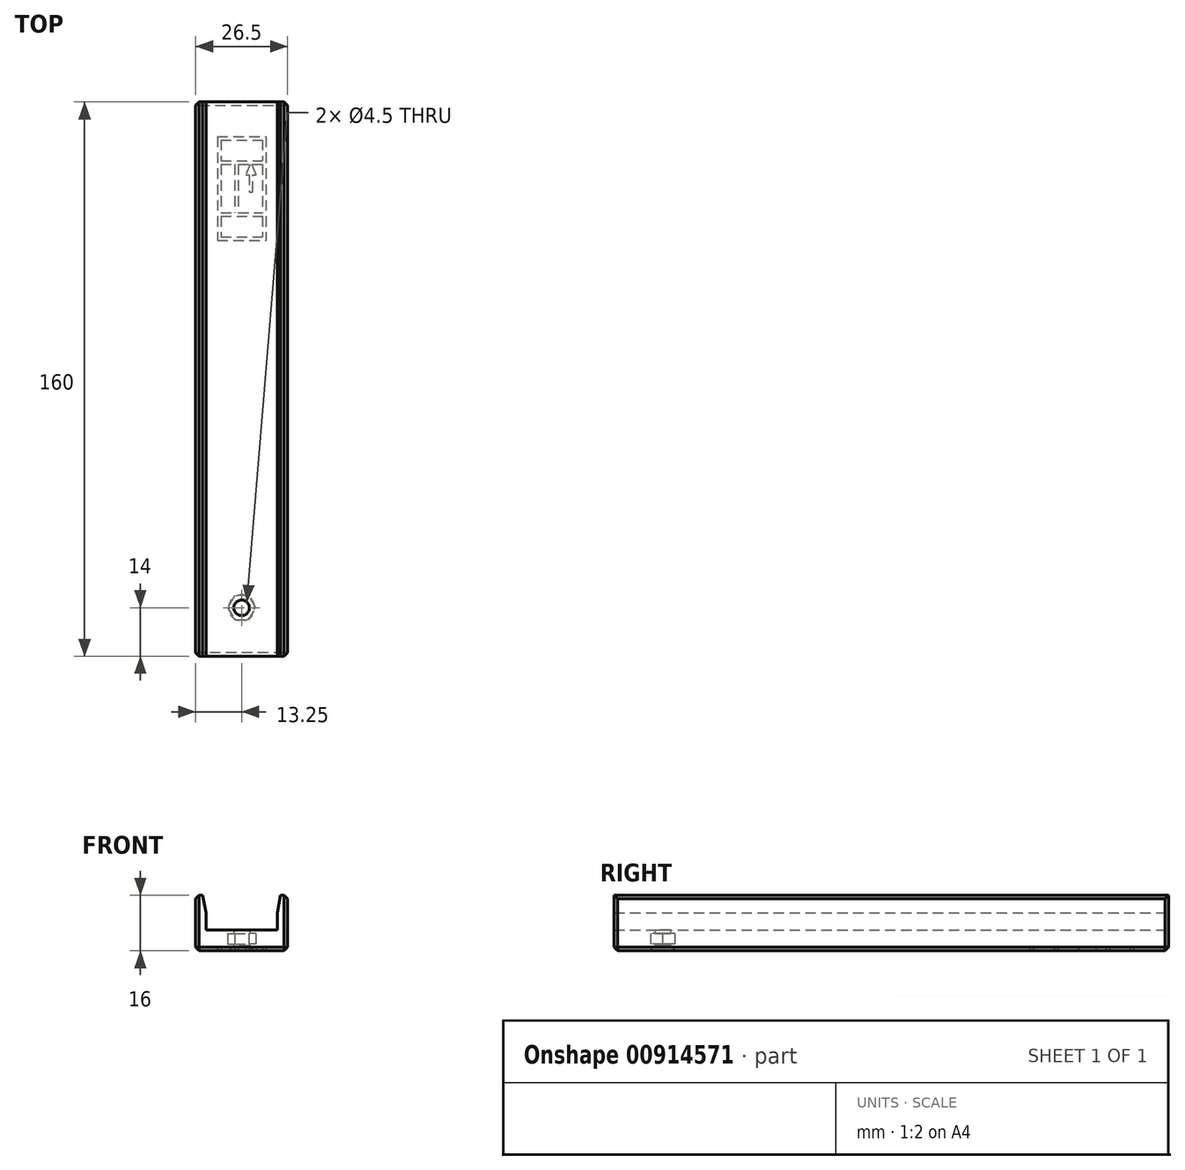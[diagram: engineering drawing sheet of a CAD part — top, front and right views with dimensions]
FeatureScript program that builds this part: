
annotation { "Feature Type Name" : "Feature", "Feature Type Description" : "" }
export const myFeature = defineFeature(function(context is Context, id is Id, definition is map)
    precondition{}
    {
        {
            var Q0;
            Q0=qCreatedBy(makeId("Front.planeOp"),FACE);
            var sketch = newSketch(context, id + "F0", { "sketchPlane" : qUnion([Q0])});
            skLineSegment(sketch, "E0", {"start": v(0, 0) * mm, "end": v(26.5, 0) * mm});
            skLineSegment(sketch, "E1", {"start": v(26.5, 0) * mm, "end": v(26.5, 16) * mm});
            skLineSegment(sketch, "E2", {"start": v(26.5, 16) * mm, "end": v(23.5, 16) * mm});
            skLineSegment(sketch, "E3", {"start": v(23.5, 16) * mm, "end": v(23.5, 6) * mm});
            skLineSegment(sketch, "E4", {"start": v(23.5, 6) * mm, "end": v(3, 6) * mm});
            skLineSegment(sketch, "E5", {"start": v(3, 6) * mm, "end": v(3, 16) * mm});
            skLineSegment(sketch, "E6", {"start": v(3, 16) * mm, "end": v(0, 16) * mm});
            skLineSegment(sketch, "E7", {"start": v(0, 16) * mm, "end": v(0, 0) * mm});
            skSolve(sketch);
        }
        {
            var Q0;
            Q0=qSketchRegion(id+"F0",true);
            extrude(context, id + "F1", {"entities" : qUnion([Q0]), "depth" : 160 * mm, "offsetDistance" : 25 * mm});
        }
        {
            var Q0;
            Q0=makeQuery(id+"F1.opExtrude","SWEPT_FACE",FACE,{"disambiguationData":[OSD([sQuery(id+"F0.wireOp",EDGE,"E0")])]});
            var sketch = newSketch(context, id + "F2", { "sketchPlane" : qUnion([Q0])});
            skCircle(sketch, "E8", {"center": v(13.25, 146) * mm, "radius": 2.25 * mm});
            skSolve(sketch);
        }
        {
            var Q0;
            Q0=qSketchRegion(id+"F2",true);
            extrude(context, id + "F3", {"entities" : qUnion([Q0]), "operationType" : NewBodyOperationType.REMOVE, "endBound" : BoundingType.THROUGH_ALL, "oppositeDirection" : true, "depth" : 25 * mm, "offsetDistance" : 25 * mm});
        }
        {
            var Q0;
            Q0=makeQuery(id+"F1.opExtrude","SWEPT_EDGE",EDGE,{"disambiguationData":[OSD([sQuery(id+"F0.wireOp",EDGE,"E2"),sQuery(id+"F0.wireOp",EDGE,"E3")])]});
            chamfer(context, id + "F4", {"entities" : qUnion([Q0]), "chamferType" : ChamferType.TWO_OFFSETS, "width1" : 5 * mm, "oppositeDirection" : false, "width2" : 1 * mm, "tangentPropagation" : true});
        }
        {
            var Q0;
            Q0=makeQuery(id+"F1.opExtrude","SWEPT_EDGE",EDGE,{"disambiguationData":[OSD([sQuery(id+"F0.wireOp",EDGE,"E5"),sQuery(id+"F0.wireOp",EDGE,"E6")])]});
            chamfer(context, id + "F5", {"entities" : qUnion([Q0]), "chamferType" : ChamferType.TWO_OFFSETS, "width1" : 1 * mm, "oppositeDirection" : false, "width2" : 5 * mm, "tangentPropagation" : true});
        }
        {
            var Q0;
            Q0=makeQuery(id+"F1.opExtrude","SWEPT_FACE",FACE,{"disambiguationData":[OSD([sQuery(id+"F0.wireOp",EDGE,"E0")])]});
            var sketch = newSketch(context, id + "F6", { "sketchPlane" : qUnion([Q0])});
            skCircle(sketch, "E9.cCircle", {"center": v(13.25, 146) * mm, "radius": 3.5 * mm, "construction": true});
            skLineSegment(sketch, "E9.0", {"start": v(11.23, 149.5) * mm, "end": v(15.27, 149.5) * mm});
            skLineSegment(sketch, "E9.1", {"start": v(15.27, 149.5) * mm, "end": v(17.3, 146) * mm});
            skLineSegment(sketch, "E9.2", {"start": v(17.3, 146) * mm, "end": v(15.27, 142.5) * mm});
            skLineSegment(sketch, "E9.3", {"start": v(15.27, 142.5) * mm, "end": v(11.23, 142.5) * mm});
            skLineSegment(sketch, "E9.4", {"start": v(11.23, 142.5) * mm, "end": v(9.2, 146) * mm});
            skLineSegment(sketch, "E9.5", {"start": v(9.2, 146) * mm, "end": v(11.23, 149.5) * mm});
            skPoint(sketch, "E9.0.midPoint", {"position": v(13.25, 149.5) * mm});
            skSolve(sketch);
        }
        {
            var Q0;
            Q0=qSketchRegion(id+"F6",true);
            extrude(context, id + "F7", {"entities" : qUnion([Q0]), "operationType" : NewBodyOperationType.REMOVE, "oppositeDirection" : true, "depth" : 5 * mm, "offsetDistance" : 25 * mm});
        }
        {
            var Q0;
            Q0=makeQuery(id+"F1.opExtrude","SWEPT_FACE",FACE,{"disambiguationData":[OSD([sQuery(id+"F0.wireOp",EDGE,"E0")])]});
            var sketch = newSketch(context, id + "F8", { "sketchPlane" : qUnion([Q0])});
            skCircle(sketch, "E10.cCircle", {"center": v(13.25, 146) * mm, "radius": 3.5 * mm, "construction": true});
            skLineSegment(sketch, "E10.0", {"start": v(11.23, 149.5) * mm, "end": v(15.27, 149.5) * mm});
            skLineSegment(sketch, "E10.1", {"start": v(15.27, 149.5) * mm, "end": v(17.3, 146) * mm});
            skLineSegment(sketch, "E10.2", {"start": v(17.3, 146) * mm, "end": v(15.27, 142.5) * mm});
            skLineSegment(sketch, "E10.3", {"start": v(15.27, 142.5) * mm, "end": v(11.23, 142.5) * mm});
            skLineSegment(sketch, "E10.4", {"start": v(11.23, 142.5) * mm, "end": v(9.2, 146) * mm});
            skLineSegment(sketch, "E10.5", {"start": v(9.2, 146) * mm, "end": v(11.23, 149.5) * mm});
            skPoint(sketch, "E10.0.midPoint", {"position": v(13.25, 149.5) * mm});
            skCircle(sketch, "E11", {"center": v(13.25, 146) * mm, "radius": 2.25 * mm});
            skSolve(sketch);
        }
        {
            var Q0;
            Q0=qSketchRegion(id+"F8",true);
            extrude(context, id + "F9", {"entities" : qUnion([Q0]), "operationType" : NewBodyOperationType.ADD, "oppositeDirection" : true, "depth" : 2 * mm, "offsetDistance" : 25 * mm});
        }
        {
            var Q0;
            Q0=makeQuery(id+"F9.opExtrude","CAP_EDGE",EDGE,{"disambiguationData":[OSD([sQuery(id+"F8.wireOp",EDGE,"E11")])],"isStart":true});
            var Q1;
            Q1=makeQuery(id+"F9.opExtrude","CAP_EDGE",EDGE,{"disambiguationData":[OSD([sQuery(id+"F8.wireOp",EDGE,"b76391ad-7746-4877-8ef7-7a4a0ac5d2b5")])],"isStart":true});
            chamfer(context, id + "F10", {"entities" : qUnion([Q0, Q1]), "width" : 1.5 * mm, "tangentPropagation" : true});
        }
        {
            var Q0;
            Q0=makeQuery(id+"F1.opExtrude","SWEPT_EDGE",EDGE,{"disambiguationData":[OSD([sQuery(id+"F0.wireOp",EDGE,"E0"),sQuery(id+"F0.wireOp",EDGE,"E7")])]});
            var Q1;
            Q1=makeQuery(id+"F1.opExtrude","CAP_EDGE",EDGE,{"disambiguationData":[OSD([sQuery(id+"F0.wireOp",EDGE,"E0")])],"isStart":true});
            var Q2;
            Q2=makeQuery(id+"F1.opExtrude","SWEPT_EDGE",EDGE,{"disambiguationData":[OSD([sQuery(id+"F0.wireOp",EDGE,"E0"),sQuery(id+"F0.wireOp",EDGE,"E1")])]});
            var Q3;
            Q3=makeQuery(id+"F1.opExtrude","CAP_EDGE",EDGE,{"disambiguationData":[OSD([sQuery(id+"F0.wireOp",EDGE,"E0")])],"isStart":false});
            var Q4;
            Q4=makeQuery(id+"F1.opExtrude","CAP_EDGE",EDGE,{"disambiguationData":[OSD([sQuery(id+"F0.wireOp",EDGE,"E7")])],"isStart":true});
            var Q5;
            Q5=makeQuery(id+"F1.opExtrude","CAP_EDGE",EDGE,{"disambiguationData":[OSD([sQuery(id+"F0.wireOp",EDGE,"E1")])],"isStart":true});
            var Q6;
            Q6=makeQuery(id+"F1.opExtrude","CAP_EDGE",EDGE,{"disambiguationData":[OSD([sQuery(id+"F0.wireOp",EDGE,"E7")])],"isStart":false});
            var Q7;
            Q7=makeQuery(id+"F1.opExtrude","CAP_EDGE",EDGE,{"disambiguationData":[OSD([sQuery(id+"F0.wireOp",EDGE,"E1")])],"isStart":false});
            var Q8;
            Q8=makeQuery(id+"F1.opExtrude","SWEPT_EDGE",EDGE,{"disambiguationData":[OSD([sQuery(id+"F0.wireOp",EDGE,"E1"),sQuery(id+"F0.wireOp",EDGE,"E2")])]});
            var Q9;
            Q9=makeQuery(id+"F1.opExtrude","SWEPT_EDGE",EDGE,{"disambiguationData":[OSD([sQuery(id+"F0.wireOp",EDGE,"E6"),sQuery(id+"F0.wireOp",EDGE,"E7")])]});
            chamfer(context, id + "F11", {"entities" : qUnion([Q0, Q1, Q2, Q3, Q4, Q5, Q6, Q7, Q8, Q9]), "width" : 1 * mm, "tangentPropagation" : true});
        }
        {
            var Q0;
            Q0=makeQuery(id+"F9.boolean.opBoolean","MERGE",FACE,{"derivedFrom":[makeQuery(id+"F1.opExtrude","SWEPT_FACE",FACE,{"disambiguationData":[OSD([sQuery(id+"F0.wireOp",EDGE,"E0")])]}),makeQuery(id+"F9.opExtrude","CAP_FACE",FACE,{"disambiguationData":[OSD([sQuery(id+"F8.wireOp",EDGE,"E10.0"),sQuery(id+"F8.wireOp",EDGE,"E10.1"),sQuery(id+"F8.wireOp",EDGE,"E10.2"),sQuery(id+"F8.wireOp",EDGE,"E10.3"),sQuery(id+"F8.wireOp",EDGE,"E10.4"),sQuery(id+"F8.wireOp",EDGE,"E10.5"),sQuery(id+"F8.wireOp",EDGE,"E11")])],"isStart":true})]});
            var sketch = newSketch(context, id + "F12", { "sketchPlane" : qUnion([Q0])});
            skLineSegment(sketch, "E12.bottom", {"start": v(6.25, 10) * mm, "end": v(20.25, 10) * mm});
            skLineSegment(sketch, "E12.top", {"start": v(7.25, 18) * mm, "end": v(11.25, 18) * mm});
            skLineSegment(sketch, "E12.left", {"start": v(6.25, 10) * mm, "end": v(6.25, 18) * mm});
            skLineSegment(sketch, "E12.right", {"start": v(20.25, 10) * mm, "end": v(20.25, 18) * mm});
            skLineSegment(sketch, "E13.bottom", {"start": v(7.25, 33) * mm, "end": v(19.25, 33) * mm});
            skLineSegment(sketch, "E13.top", {"start": v(6.25, 40) * mm, "end": v(20.25, 40) * mm});
            skLineSegment(sketch, "E13.left", {"start": v(6.25, 33) * mm, "end": v(6.25, 40) * mm});
            skLineSegment(sketch, "E13.right", {"start": v(20.25, 33) * mm, "end": v(20.25, 40) * mm});
            skLineSegment(sketch, "E14", {"start": v(6.25, 18) * mm, "end": v(6.25, 33) * mm});
            skLineSegment(sketch, "E15", {"start": v(20.25, 18) * mm, "end": v(20.25, 32) * mm});
            skLineSegment(sketch, "E16", {"start": v(11.25, 18) * mm, "end": v(11.25, 32) * mm});
            skLineSegment(sketch, "E17.0", {"start": v(7.25, 18) * mm, "end": v(7.25, 32) * mm});
            skLineSegment(sketch, "E18.0", {"start": v(12.25, 18) * mm, "end": v(12.25, 32) * mm});
            skLineSegment(sketch, "E19.0", {"start": v(7.25, 32) * mm, "end": v(11.25, 32) * mm});
            skLineSegment(sketch, "E20.0", {"start": v(7.25, 39) * mm, "end": v(19.25, 39) * mm});
            skLineSegment(sketch, "E21.0", {"start": v(7.25, 11) * mm, "end": v(19.25, 11) * mm});
            skLineSegment(sketch, "E22.0", {"start": v(7.25, 11) * mm, "end": v(7.25, 17) * mm});
            skLineSegment(sketch, "E23.0", {"start": v(7.25, 33) * mm, "end": v(7.25, 39) * mm});
            skLineSegment(sketch, "E24.0", {"start": v(7.25, 17) * mm, "end": v(19.25, 17) * mm});
            skLineSegment(sketch, "E25.0", {"start": v(19.25, 11) * mm, "end": v(19.25, 17) * mm});
            skLineSegment(sketch, "E26.0", {"start": v(19.25, 18) * mm, "end": v(19.25, 32) * mm});
            skLineSegment(sketch, "E27.0", {"start": v(19.25, 33) * mm, "end": v(19.25, 39) * mm});
            skLineSegment(sketch, "E28.trimOffspring", {"start": v(12.25, 18) * mm, "end": v(15.72, 18) * mm});
            skLineSegment(sketch, "E29.trimOffspring", {"start": v(12.25, 32) * mm, "end": v(19.25, 32) * mm});
            skPoint(sketch, "E30.orphan", {"position": v(11.25, 33) * mm});
            skLineSegment(sketch, "E31", {"start": v(20.25, 32) * mm, "end": v(20.25, 33) * mm});
            skPoint(sketch, "E32", {"position": v(13.25, 10) * mm});
            skLineSegment(sketch, "E33", {"start": v(15.72, 18) * mm, "end": v(14.47, 21) * mm});
            skLineSegment(sketch, "E34", {"start": v(14.47, 21) * mm, "end": v(15.47, 21) * mm});
            skLineSegment(sketch, "E35", {"start": v(15.47, 21) * mm, "end": v(15.47, 26) * mm});
            skLineSegment(sketch, "E36", {"start": v(15.47, 26) * mm, "end": v(16.47, 26) * mm});
            skLineSegment(sketch, "E37", {"start": v(16.47, 26) * mm, "end": v(16.47, 21) * mm});
            skLineSegment(sketch, "E38", {"start": v(16.47, 21) * mm, "end": v(17.47, 21) * mm});
            skLineSegment(sketch, "E39", {"start": v(17.47, 21) * mm, "end": v(16.22, 18) * mm});
            skLineSegment(sketch, "E40.trimOffspring", {"start": v(16.22, 18) * mm, "end": v(19.25, 18) * mm});
            skSolve(sketch);
        }
        {
            var Q0;
            Q0 = qSketchRegion(id + "F12", true);
            extrude(context, id + "F13", {"entities" : qUnion([Q0]), "operationType" : NewBodyOperationType.REMOVE, "oppositeDirection" : true, "depth" : 1 * mm, "offsetDistance" : 25 * mm});
        }
    });
